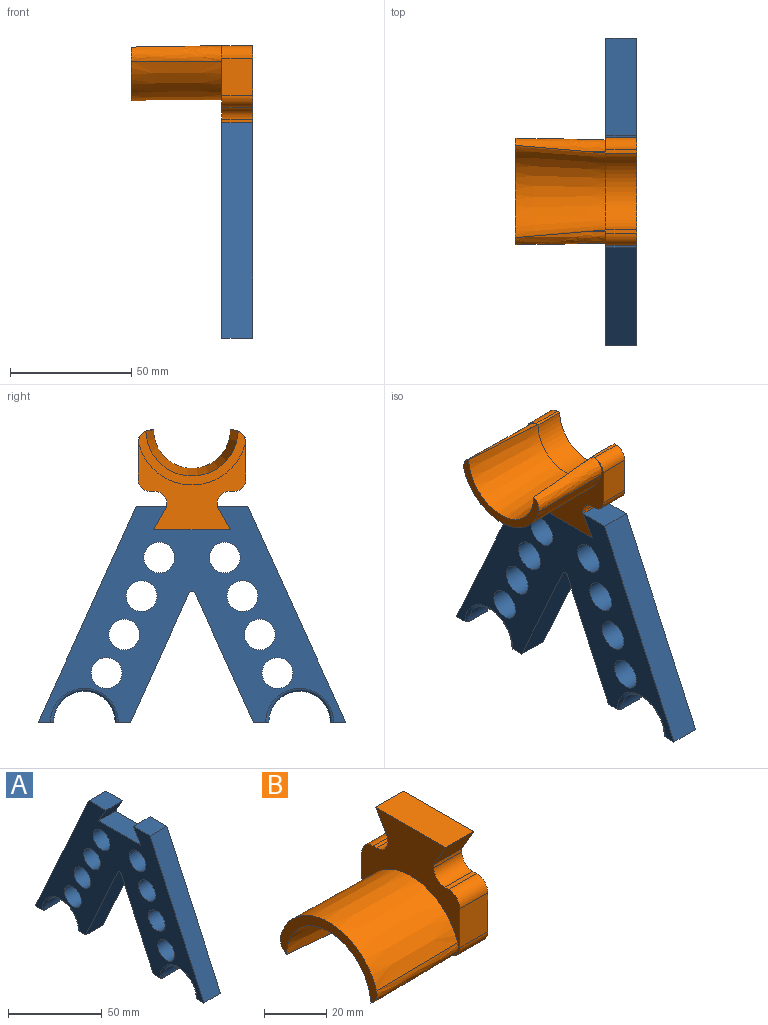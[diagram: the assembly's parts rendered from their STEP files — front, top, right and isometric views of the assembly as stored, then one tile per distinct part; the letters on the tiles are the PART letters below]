
ASSEMBLY  parts=2 mates=1
PART A: 30 faces, bbox 12.7x127x88.9 mm
  f0: plane 53.32x24.24mm, normal (0,0.91,-0.41), area 743.8mm2, adj f11,f12,f13,f27
  f1: plane 31.75x12.7mm, normal (0,0,1), area 403.2mm2, adj f2,f12,f13,f15
  f2: plane 12.7x9.53mm, normal (0,0.87,-0.5), area 139.7mm2, adj f1,f3,f12,f13
  f3: plane 12.7x12.7mm, normal (0,0,1), area 161.3mm2, adj f2,f4,f12,f13
  f4: plane 88.9x40.42mm, normal (0,-0.91,0.41), area 1240.3mm2, adj f3,f5,f12,f13
  f5: plane 12.7x6.35mm, normal (0,0,-1), area 80mm2, adj f4,f6,f12,f13,f28,f29
  f6: cylinder r=12.7mm len=25.4mm, axis (-1,0,0), area 405.4mm2, adj f5,f11,f28,f29
  f7: cylinder r=6.35mm len=12.7mm, axis (-1,0,0), area 506.7mm2, adj f12,f13
  f8: cylinder r=6.35mm len=12.7mm, axis (-1,0,0), area 506.7mm2, adj f12,f13
  f9: cylinder r=6.35mm len=12.7mm, axis (-1,0,0), area 506.7mm2, adj f12,f13
  f10: cylinder r=6.35mm len=12.7mm, axis (-1,0,0), area 506.7mm2, adj f12,f13
  f11: plane 12.7x6.35mm, normal (0,0,-1), area 80mm2, adj f0,f6,f12,f13,f28,f29
  f12: plane 127x88.9mm, normal (1,0,0), area 4402.9mm2, adj f0,f1,f2,f3,f4,f5,f7,f8
  f13: plane 127x88.9mm, normal (-1,0,0), area 4402.9mm2, adj f0,f1,f2,f3,f4,f5,f7,f8
  f14: plane 53.32x24.24mm, normal (0,-0.91,-0.41), area 743.8mm2, adj f12,f13,f24,f27
  f15: plane 12.7x9.53mm, normal (0,-0.87,-0.5), area 139.7mm2, adj f1,f12,f13,f16
  f16: plane 12.7x12.7mm, normal (0,0,1), area 161.3mm2, adj f12,f13,f15,f17
  f17: plane 88.9x40.42mm, normal (0,0.91,0.41), area 1240.3mm2, adj f12,f13,f16,f18
  f18: plane 12.7x6.35mm, normal (0,0,-1), area 80mm2, adj f12,f13,f17,f19,f25,f26
  f19: cylinder r=12.7mm len=25.4mm, axis (-1,0,0), area 405.4mm2, adj f18,f24,f25,f26
  f20: cylinder r=6.35mm len=12.7mm, axis (-1,0,0), area 506.7mm2, adj f12,f13
  f21: cylinder r=6.35mm len=12.7mm, axis (-1,0,0), area 506.7mm2, adj f12,f13
  f22: cylinder r=6.35mm len=12.7mm, axis (-1,0,0), area 506.7mm2, adj f12,f13
  f23: cylinder r=6.35mm len=12.7mm, axis (-1,0,0), area 506.7mm2, adj f12,f13
  f24: plane 12.7x6.35mm, normal (0,0,-1), area 80mm2, adj f12,f13,f14,f19,f25,f26
  f25: torus R=13.97mm, axis (1,0,0), area 82.5mm2, adj f13,f18,f19,f24
  f26: torus R=13.97mm, axis (1,0,0), area 82.5mm2, adj f12,f18,f19,f24
  f27: cylinder r=1.27mm len=12.7mm, axis (1,0,0), area 36.9mm2, adj f0,f12,f13,f14
  f28: torus R=13.97mm, axis (1,0,0), area 82.5mm2, adj f5,f6,f11,f13
  f29: torus R=13.97mm, axis (1,0,0), area 82.5mm2, adj f5,f6,f11,f12
PART B: 25 faces, bbox 69.1x48.2x41.6 mm
  f0: cone r=15.88mm half-angle=4.9deg, axis (-1,0,0), area 2039.8mm2, adj f2,f3,f4,f5,f6,f10
  f1: cone r=22.23mm half-angle=0.8deg, axis (-1,0,0), area 2136.9mm2, adj f2,f5,f6,f7
  f2: plane 44.34x22.62mm, normal (-1,0,0), area 225.1mm2, adj f0,f1,f5,f6
  f3: plane 19.73x1.27mm, normal (0,0,-1), area 17.9mm2, adj f0,f6,f7,f10,f14,f19
  f4: plane 19.73x1.27mm, normal (0,0,-1), area 17.9mm2, adj f0,f5,f7,f10,f14,f23
  f5: bspline ~68.75x7.77mm, area 321.3mm2, adj f0,f1,f2,f4,f7
  f6: bspline ~68.75x7.77mm, area 321.3mm2, adj f0,f1,f2,f3,f7
  f7: plane 44.74x41.56mm, normal (-1,0,0), area 741mm2, adj f1,f3,f4,f5,f6,f8,f9,f11
  f8: plane 12.7x1.69mm, normal (0,0,1), area 21.5mm2, adj f7,f14,f22,f24
  f9: plane 15.24x12.7mm, normal (0,-1,0), area 193.5mm2, adj f7,f14,f22,f23
  f10: cylinder r=15.88mm len=31.75mm, axis (-1,0,0), area 633.4mm2, adj f0,f3,f4,f14
  f11: plane 31.75x12.7mm, normal (0,0,1), area 403.2mm2, adj f7,f12,f14,f17
  f12: plane 12.7x9.53mm, normal (0,-0.87,-0.5), area 139.7mm2, adj f7,f11,f13,f14
  f13: plane 12.7x1.27mm, normal (0,-1,0), area 16.1mm2, adj f7,f12,f14,f24
  f14: plane 44.45x41.28mm, normal (1,0,0), area 1103.9mm2, adj f3,f4,f8,f9,f10,f11,f12,f13
  f15: plane 12.7x1.69mm, normal (0,0,1), area 21.5mm2, adj f7,f14,f20,f21
  f16: plane 15.24x12.7mm, normal (0,1,0), area 193.5mm2, adj f7,f14,f19,f21
  f17: plane 12.7x9.53mm, normal (0,0.87,-0.5), area 139.7mm2, adj f7,f11,f14,f18
  f18: plane 12.7x1.27mm, normal (0,1,0), area 16.1mm2, adj f7,f14,f17,f20
  f19: cylinder r=5.08mm len=12.7mm, axis (-1,0,0), area 101.3mm2, adj f3,f7,f14,f16
  f20: cylinder r=5.08mm len=12.7mm, axis (1,0,0), area 101.3mm2, adj f7,f14,f15,f18
  f21: cylinder r=5.08mm len=12.7mm, axis (-1,0,0), area 101.3mm2, adj f7,f14,f15,f16
  f22: cylinder r=5.08mm len=12.7mm, axis (-1,0,0), area 101.3mm2, adj f7,f8,f9,f14
  f23: cylinder r=5.08mm len=12.7mm, axis (-1,0,0), area 101.3mm2, adj f4,f7,f9,f14
  f24: cylinder r=5.08mm len=12.7mm, axis (1,0,0), area 101.3mm2, adj f7,f8,f13,f14
PLACE A t=(-89.37,-5.27,59.51)mm
PLACE B rot(axis=(1,0,0),180deg) t=(-89.37,-5.27,180.16)mm
MATE fastened B.f11 <-> A.f1  axis (0,0,-1) through (-83.02,-5.27,138.88)mm
